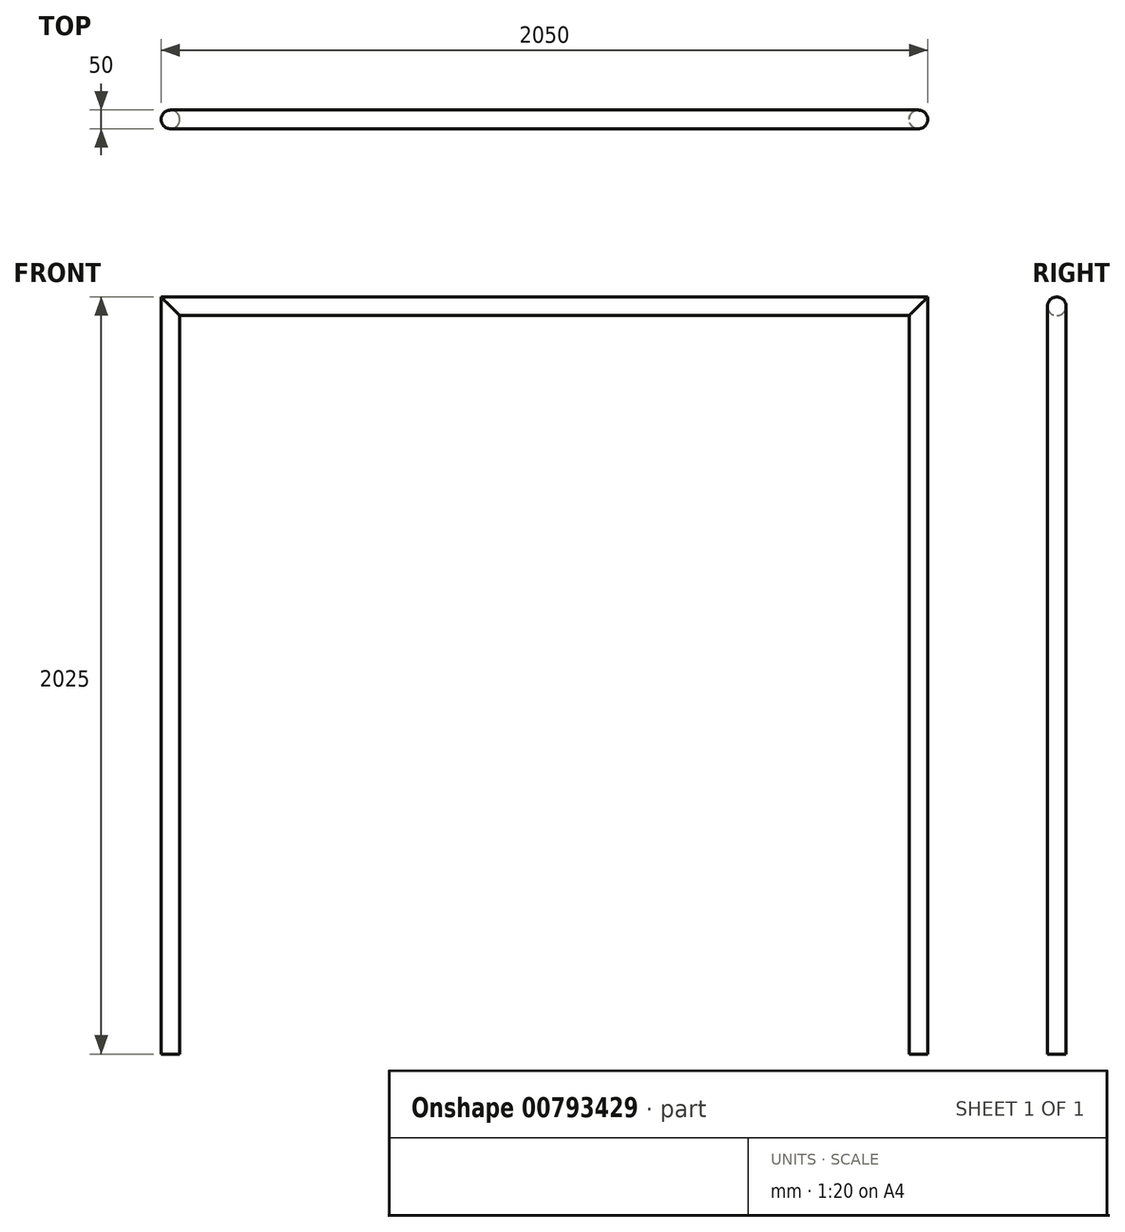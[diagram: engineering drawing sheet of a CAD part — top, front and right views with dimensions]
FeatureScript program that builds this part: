
annotation { "Feature Type Name" : "Feature", "Feature Type Description" : "" }
export const myFeature = defineFeature(function(context is Context, id is Id, definition is map)
    precondition{}
    {
        {
            var Q0;
            Q0=qCreatedBy(makeId("Front.planeOp"),FACE);
            var sketch = newSketch(context, id + "F0", { "sketchPlane" : qUnion([Q0])});
            skLineSegment(sketch, "E0", {"start": v(-2463.4, 0) * mm, "end": v(-2463.4, 2000) * mm});
            skLineSegment(sketch, "E1", {"start": v(-2463.4, 2000) * mm, "end": v(-463.4, 2000) * mm});
            skLineSegment(sketch, "E2", {"start": v(-463.4, 2000) * mm, "end": v(-463.4, 0) * mm});
            skSolve(sketch);
        }
        {
            var Q0;
            Q0=qCreatedBy(makeId("Top.planeOp"),FACE);
            var sketch = newSketch(context, id + "F1", { "sketchPlane" : qUnion([Q0])});
            skCircle(sketch, "E3", {"center": v(-463.4, 0) * mm, "radius": 25 * mm});
            skSolve(sketch);
        }
        {
            var Q0;
            Q0=qCreatedBy(makeId("Front.planeOp"),FACE);
            var sketch = newSketch(context, id + "F2", { "sketchPlane" : qUnion([Q0])});
            skLineSegment(sketch, "E4.top", {"start": v(-2463.4, 2000) * mm, "end": v(-463.4, 2000) * mm});
            skLineSegment(sketch, "E4.left", {"start": v(-2463.4, 0) * mm, "end": v(-2463.4, 2000) * mm});
            skLineSegment(sketch, "E4.right", {"start": v(-463.4, 0) * mm, "end": v(-463.4, 2000) * mm});
            skLineSegment(sketch, "E5", {"start": v(-2463.4, 2000) * mm, "end": v(-2130.1, 2000) * mm});
            skLineSegment(sketch, "E6", {"start": v(-463.4, 2000) * mm, "end": v(-796.7, 2000) * mm});
            skLineSegment(sketch, "E7", {"start": v(-463.4, 2000) * mm, "end": v(-1296.7, 2000) * mm});
            skLineSegment(sketch, "E8", {"start": v(-2463.4, 2000) * mm, "end": v(-1630.1, 2000) * mm});
            skSolve(sketch);
        }
        {
            var Q0;
            Q0=qCreatedBy(makeId("Top.planeOp"),FACE);
            var sketch = newSketch(context, id + "F3", { "sketchPlane" : qUnion([Q0])});
            skCircle(sketch, "E9", {"center": v(-2463.4, 0) * mm, "radius": 25 * mm});
            skSolve(sketch);
        }
        {
            var Q0;
            Q0=makeQuery(id+"F3.imprint","IMPRINT",FACE,{"disambiguationData":[TD([[makeQuery(id+"F3.imprint","IMPRINT",EDGE,{"derivedFrom":sQuery(id+"F3.wireOp",EDGE,"E9")}),1.0]])]});
            var Q1;
            Q1=sQuery(id+"F2.wireOp",EDGE,"E4.left");
            var Q2;
            Q2=sQuery(id+"F2.wireOp",EDGE,"E4.top");
            var Q3;
            Q3=sQuery(id+"F2.wireOp",EDGE,"E4.right");
            sweep(context, id + "F4", {"profiles" : qUnion([Q0]), "path" : qUnion([Q1, Q2, Q3])});
        }
    });
